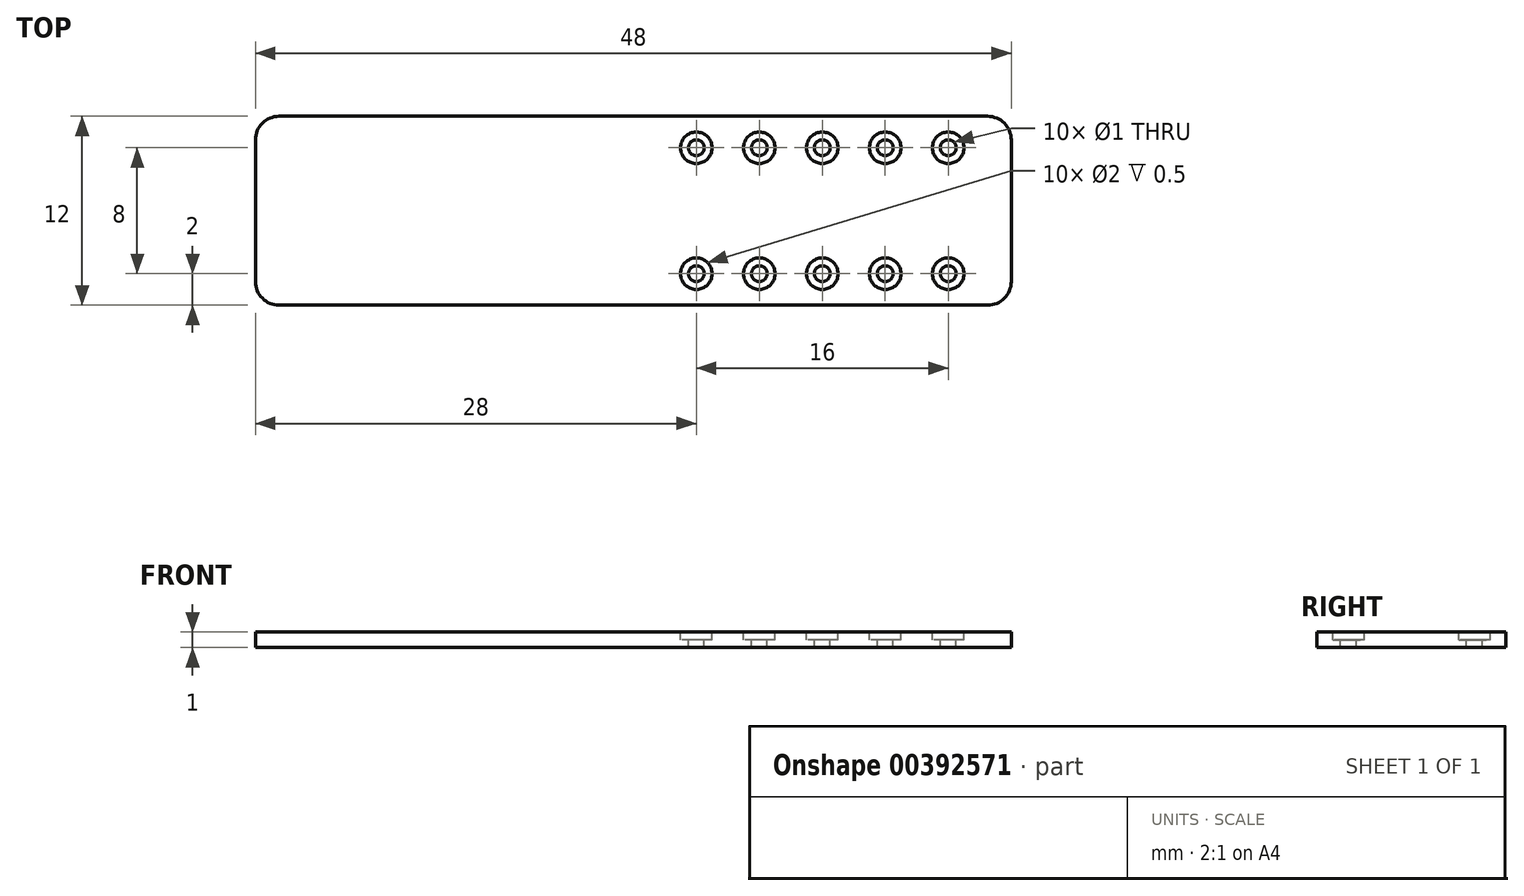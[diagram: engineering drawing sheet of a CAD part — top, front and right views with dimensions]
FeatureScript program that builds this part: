
annotation { "Feature Type Name" : "Feature", "Feature Type Description" : "" }
export const myFeature = defineFeature(function(context is Context, id is Id, definition is map)
    precondition{}
    {
        {
            var Q0;
            Q0=qCreatedBy(makeId("Top.planeOp"),FACE);
            var sketch = newSketch(context, id + "F0", { "sketchPlane" : qUnion([Q0])});
            skLineSegment(sketch, "E0.bottom", {"start": v(-24, 6) * mm, "end": v(24, 6) * mm});
            skLineSegment(sketch, "E0.top", {"start": v(-24, -6) * mm, "end": v(24, -6) * mm});
            skLineSegment(sketch, "E0.left", {"start": v(-24, 6) * mm, "end": v(-24, -6) * mm});
            skLineSegment(sketch, "E0.right", {"start": v(24, 6) * mm, "end": v(24, -6) * mm});
            skPoint(sketch, "E0.middle", {"position": v(0, 0) * mm});
            skSolve(sketch);
        }
        {
            var Q0;
            Q0=makeQuery(id+"F0.imprint","IMPRINT",FACE,{"disambiguationData":[TD([[makeQuery(id+"F0.imprint","IMPRINT",EDGE,{"derivedFrom":sQuery(id+"F0.wireOp",EDGE,"E0.bottom")}),-1.0]])]});
            extrude(context, id + "F1", {"entities" : qUnion([Q0]), "depth" : 1 * mm});
        }
        {
            var Q0;
            Q0=makeQuery(id+"F1.opExtrude","CAP_FACE",FACE,{"disambiguationData":[OSD([sQuery(id+"F0.wireOp",EDGE,"E0.bottom"),sQuery(id+"F0.wireOp",EDGE,"E0.top"),sQuery(id+"F0.wireOp",EDGE,"E0.left"),sQuery(id+"F0.wireOp",EDGE,"E0.right")])],"isStart":false});
            var sketch = newSketch(context, id + "F2", { "sketchPlane" : qUnion([Q0])});
            skLineSegment(sketch, "E1", {"start": v(0, 6) * mm, "end": v(0, -6) * mm, "construction": true});
            skLineSegment(sketch, "E2", {"start": v(8, 6) * mm, "end": v(8, -6) * mm, "construction": true});
            skLineSegment(sketch, "E3", {"start": v(12, 6) * mm, "end": v(12, -6) * mm, "construction": true});
            skLineSegment(sketch, "E4", {"start": v(16, 6) * mm, "end": v(16, -6) * mm, "construction": true});
            skLineSegment(sketch, "E5", {"start": v(-8, 6) * mm, "end": v(-8, -6) * mm, "construction": true});
            skLineSegment(sketch, "E6", {"start": v(-12, 6) * mm, "end": v(-12, -6) * mm, "construction": true});
            skLineSegment(sketch, "E7", {"start": v(-16, 6) * mm, "end": v(-16, -6) * mm, "construction": true});
            skLineSegment(sketch, "E8", {"start": v(-24, 0) * mm, "end": v(24, 0) * mm, "construction": true});
            skLineSegment(sketch, "E9", {"start": v(24, 4) * mm, "end": v(-24, 4) * mm, "construction": true});
            skLineSegment(sketch, "E10", {"start": v(24, -4) * mm, "end": v(-24, -4) * mm, "construction": true});
            skLineSegment(sketch, "E11", {"start": v(4, 6) * mm, "end": v(4, -6) * mm, "construction": true});
            skLineSegment(sketch, "E12", {"start": v(-4, 6) * mm, "end": v(-4, -6) * mm, "construction": true});
            skLineSegment(sketch, "E13", {"start": v(20, 6) * mm, "end": v(20, -6) * mm, "construction": true});
            skLineSegment(sketch, "E14", {"start": v(-20, 6) * mm, "end": v(-20, -6) * mm, "construction": true});
            skPoint(sketch, "E15", {"position": v(0, 4) * mm});
            skPoint(sketch, "E16", {"position": v(4, 4) * mm});
            skPoint(sketch, "E17", {"position": v(8, 4) * mm});
            skPoint(sketch, "E18", {"position": v(12, 4) * mm});
            skPoint(sketch, "E19", {"position": v(16, 4) * mm});
            skPoint(sketch, "E20", {"position": v(20, 4) * mm});
            skPoint(sketch, "E21", {"position": v(20, 0) * mm});
            skPoint(sketch, "E22", {"position": v(20, -4) * mm});
            skPoint(sketch, "E23", {"position": v(16, -4) * mm});
            skPoint(sketch, "E24", {"position": v(16, 0) * mm});
            skPoint(sketch, "E25", {"position": v(12, 0) * mm});
            skPoint(sketch, "E26", {"position": v(12, -4) * mm});
            skPoint(sketch, "E27", {"position": v(8, -4) * mm});
            skPoint(sketch, "E28", {"position": v(8, 0) * mm});
            skPoint(sketch, "E29", {"position": v(4, 0) * mm});
            skPoint(sketch, "E30", {"position": v(0, -4) * mm});
            skPoint(sketch, "E31", {"position": v(0, 0) * mm});
            skPoint(sketch, "E32", {"position": v(-4, 4) * mm});
            skPoint(sketch, "E33", {"position": v(-4, 0) * mm});
            skPoint(sketch, "E34", {"position": v(-4, -4) * mm});
            skPoint(sketch, "E35", {"position": v(-8, -4) * mm});
            skPoint(sketch, "E36", {"position": v(-8, 0) * mm});
            skPoint(sketch, "E37", {"position": v(-8, 4) * mm});
            skPoint(sketch, "E38", {"position": v(-12, 4) * mm});
            skPoint(sketch, "E39", {"position": v(-12, 0) * mm});
            skPoint(sketch, "E40", {"position": v(-16, -4) * mm});
            skPoint(sketch, "E41", {"position": v(-16, 0) * mm});
            skPoint(sketch, "E42", {"position": v(-20, 4) * mm});
            skPoint(sketch, "E43", {"position": v(-20, 0) * mm});
            skPoint(sketch, "E44", {"position": v(-20, -4) * mm});
            skPoint(sketch, "E45", {"position": v(-12, -4) * mm});
            skPoint(sketch, "E46", {"position": v(-16, 4) * mm});
            skPoint(sketch, "E47", {"position": v(4, -4) * mm});
            skSolve(sketch);
        }
        {
            var Q0;
            Q0=makeQuery(id+"F1.opExtrude","SWEPT_EDGE",EDGE,{"disambiguationData":[OSD([sQuery(id+"F0.wireOp",EDGE,"E0.top"),sQuery(id+"F0.wireOp",EDGE,"E0.right")])]});
            var Q1;
            Q1=makeQuery(id+"F1.opExtrude","SWEPT_EDGE",EDGE,{"disambiguationData":[OSD([sQuery(id+"F0.wireOp",EDGE,"E0.bottom"),sQuery(id+"F0.wireOp",EDGE,"E0.right")])]});
            var Q2;
            Q2=makeQuery(id+"F1.opExtrude","SWEPT_EDGE",EDGE,{"disambiguationData":[OSD([sQuery(id+"F0.wireOp",EDGE,"E0.bottom"),sQuery(id+"F0.wireOp",EDGE,"E0.left")])]});
            var Q3;
            Q3=makeQuery(id+"F1.opExtrude","SWEPT_EDGE",EDGE,{"disambiguationData":[OSD([sQuery(id+"F0.wireOp",EDGE,"E0.top"),sQuery(id+"F0.wireOp",EDGE,"E0.left")])]});
            fillet(context, id + "F3", {"entities" : qUnion([Q0, Q1, Q2, Q3]), "radius" : 1.5 * mm, "tangentPropagation" : true, "allowEdgeOverflow" : false});
        }
        {
            var Q0;
            Q0=makeQuery(id+"F2.imprint","IMPRINT",FACE,{"disambiguationData":[TD([[makeQuery(id+"F2.imprint","IMPRINT",EDGE,{"derivedFrom":makeQuery(id+"F1.opExtrude","CAP_EDGE",EDGE,{"disambiguationData":[OSD([sQuery(id+"F0.wireOp",EDGE,"E0.bottom")])],"isStart":false})}),-1.0]])]});
            var sketch = newSketch(context, id + "F4", { "sketchPlane" : qUnion([Q0])});
            skCircle(sketch, "E48", {"center": v(4, 4) * mm, "radius": 0.5 * mm});
            skCircle(sketch, "E49", {"center": v(8, 4) * mm, "radius": 0.5 * mm});
            skCircle(sketch, "E50", {"center": v(12, 4) * mm, "radius": 0.5 * mm});
            skCircle(sketch, "E51", {"center": v(16, 4) * mm, "radius": 0.5 * mm});
            skCircle(sketch, "E52", {"center": v(20, 4) * mm, "radius": 0.5 * mm});
            skCircle(sketch, "E53", {"center": v(20, -4) * mm, "radius": 0.5 * mm});
            skCircle(sketch, "E54", {"center": v(16, -4) * mm, "radius": 0.5 * mm});
            skCircle(sketch, "E55", {"center": v(12, -4) * mm, "radius": 0.5 * mm});
            skCircle(sketch, "E56", {"center": v(8, -4) * mm, "radius": 0.5 * mm});
            skCircle(sketch, "E57", {"center": v(4, -4) * mm, "radius": 0.5 * mm});
            skSolve(sketch);
        }
        {
            var Q0;
            Q0=makeQuery(id+"F2.imprint","IMPRINT",FACE,{"disambiguationData":[TD([[makeQuery(id+"F2.imprint","IMPRINT",EDGE,{"derivedFrom":makeQuery(id+"F1.opExtrude","CAP_EDGE",EDGE,{"disambiguationData":[OSD([sQuery(id+"F0.wireOp",EDGE,"E0.bottom")])],"isStart":false})}),-1.0]])]});
            var sketch = newSketch(context, id + "F5", { "sketchPlane" : qUnion([Q0])});
            skCircle(sketch, "E58", {"center": v(4, 4) * mm, "radius": 1 * mm});
            skCircle(sketch, "E59", {"center": v(8, 4) * mm, "radius": 1 * mm});
            skCircle(sketch, "E60", {"center": v(12, 4) * mm, "radius": 1 * mm});
            skCircle(sketch, "E61", {"center": v(16, 4) * mm, "radius": 1 * mm});
            skCircle(sketch, "E62", {"center": v(20, 4) * mm, "radius": 1 * mm});
            skCircle(sketch, "E63", {"center": v(20, -4) * mm, "radius": 1 * mm});
            skCircle(sketch, "E64", {"center": v(16, -4) * mm, "radius": 1 * mm});
            skCircle(sketch, "E65", {"center": v(12, -4) * mm, "radius": 1 * mm});
            skCircle(sketch, "E66", {"center": v(8, -4) * mm, "radius": 1 * mm});
            skCircle(sketch, "E67", {"center": v(4, -4) * mm, "radius": 1 * mm});
            skSolve(sketch);
        }
        {
            var Q0;
            Q0 = qSketchRegion(id + "F4", true);
            extrude(context, id + "F6", {"entities" : qUnion([Q0]), "operationType" : NewBodyOperationType.REMOVE, "oppositeDirection" : true, "depth" : 1 * mm});
        }
        {
            var Q0;
            Q0 = qSketchRegion(id + "F5", true);
            extrude(context, id + "F7", {"entities" : qUnion([Q0]), "operationType" : NewBodyOperationType.REMOVE, "oppositeDirection" : true, "depth" : .5 * mm});
        }
    });
